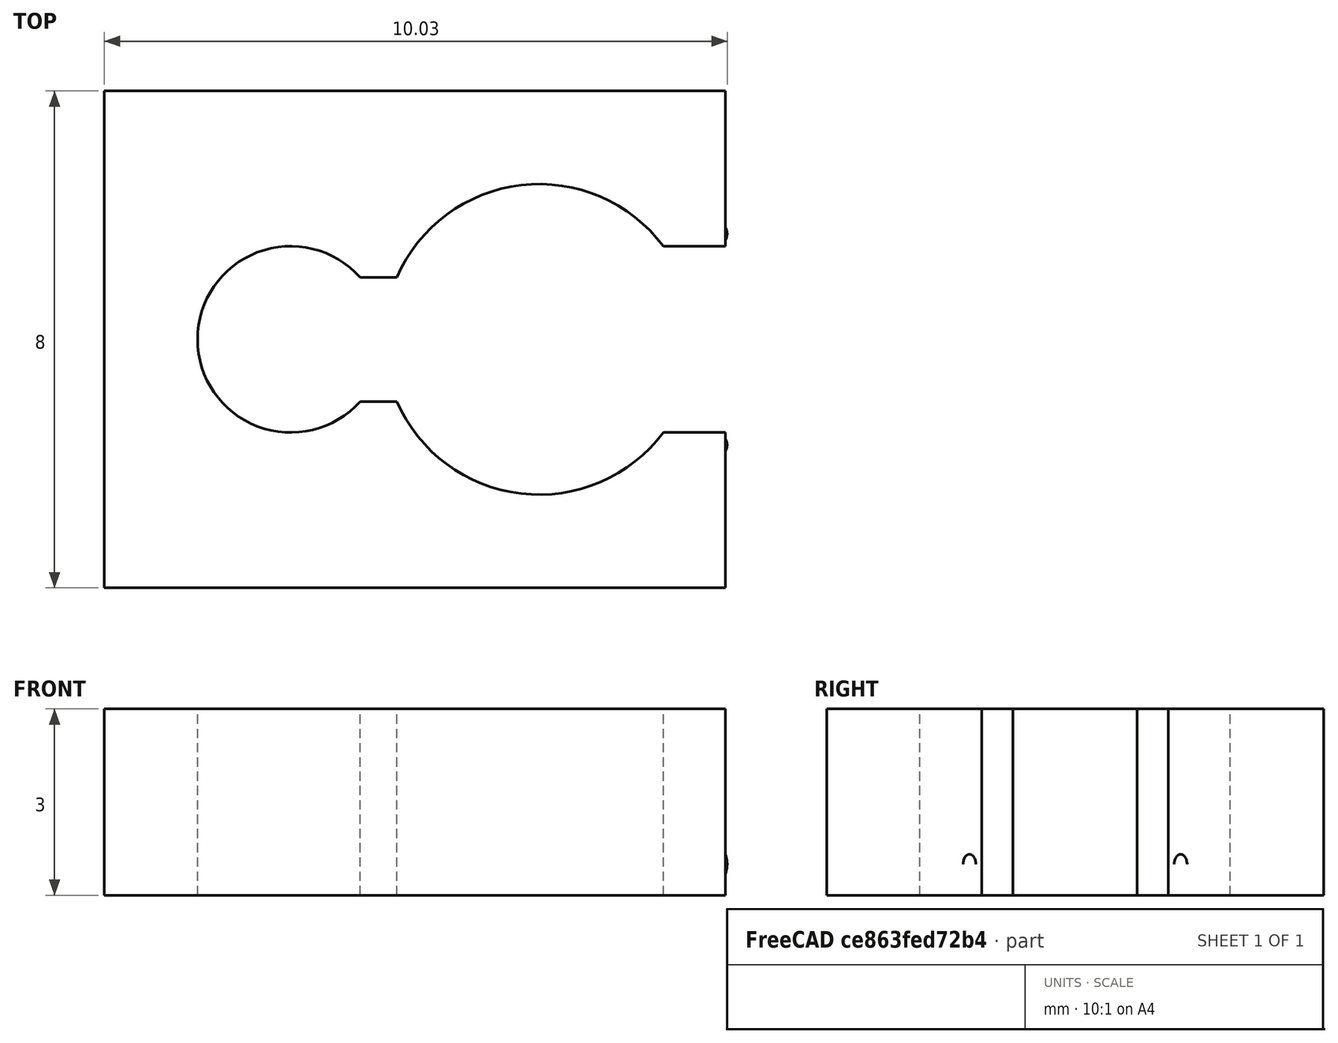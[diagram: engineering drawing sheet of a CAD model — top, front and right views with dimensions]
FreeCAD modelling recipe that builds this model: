
FCSTD DOCUMENT  (FreeCAD 0.16R)
Label: Auriculares Edu V3
License: All rights reserved
LicenseURL: http://en.wikipedia.org/wiki/All_rights_reserved
objects: Part::Cut×8, Part::Box×5, Part::Cylinder×4, Part::Torus×2, Part::MultiFuse×2, PartDesign::Fillet×1
note: 22 computed .brp shape members not serialized (recipe doc carries the construction recipe); baked Part::Feature solids carry a one-line shape summary decoded from their .brp

FEATURE [Part::Torus] Torus  label="Toro"
  Angle1 = -180
  Angle2 = 180
  Angle3 = 360
  Placement = pos=(-1,0,0) rot=(0,0,1;0rad)
  Radius1 = 3
  Radius2 = 0.5
FEATURE [Part::Torus] Torus001  label="Toro001"
  Angle1 = -180
  Angle2 = 180
  Angle3 = 360
  Placement = pos=(-5,0,0) rot=(0,0,1;0rad)
  Radius1 = 2
  Radius2 = 0.5
FEATURE [Part::MultiFuse] Fusion
  Shapes = -> [Torus001,Torus]
FEATURE [Part::Cylinder] Cylinder  label="Cilindro"
  Angle = 360
  Height = 10
  Placement = pos=(-5,0,-4) rot=(0,0,1;0rad)
  Radius = 1.5
FEATURE [Part::Cut] Cut
  Base = -> Fusion
  Tool = -> Cylinder
FEATURE [Part::Cylinder] Cylinder001  label="Cilindro001"
  Angle = 360
  Height = 10
  Placement = pos=(-1,0,-9) rot=(0,0,1;0rad)
  Radius = 2.5
FEATURE [Part::Cut] Cut001
  Base = -> Cut
  Tool = -> Cylinder001
FEATURE [Part::Box] Box  label="Cubo"
  Height = 5
  Length = 3
  Placement = pos=(-4,-0.5,-3) rot=(0,0,1;0rad)
  Width = 1
FEATURE [Part::Cut] Cut002
  Base = -> Cut001
  Tool = -> Box
FEATURE [Part::Box] Box001  label="Cubo001"
  Height = 10
  Length = 4
  Placement = pos=(0,-1.5,-6) rot=(0,0,1;0rad)
  Width = 3
FEATURE [Part::Cut] Cut003
  Base = -> Cut002
  Tool = -> Box001
FEATURE [PartDesign::Fillet] Fillet
  Base = -> Cut003 [Edge34,Edge14,Edge23,Edge25]
  Radius = 0.5
FEATURE [Part::Box] Box002  label="Cubo002"
  Height = 3
  Length = 10
  Placement = pos=(-8,-4,-0.5) rot=(0,0,1;0rad)
  Width = 8
FEATURE [Part::Cylinder] Cylinder002  label="Cilindro002"
  Angle = 360
  Height = 10
  Placement = pos=(-5,0,-1) rot=(0,0,1;0rad)
  Radius = 1.5
FEATURE [Part::MultiFuse] Fusion001
  Shapes = -> [Box002,Fillet]
FEATURE [Part::Cylinder] Cylinder003  label="Cilindro003"
  Angle = 360
  Height = 10
  Placement = pos=(-1,0,-1) rot=(0,0,1;0rad)
  Radius = 2.5
FEATURE [Part::Cut] Cut004
  Base = -> Fusion001
  Tool = -> Cylinder002
FEATURE [Part::Cut] Cut005
  Base = -> Cut004
  Tool = -> Cylinder003
FEATURE [Part::Box] Box003  label="Cubo003"
  Height = 10
  Length = 9
  Placement = pos=(0,-1.5,-3) rot=(0,0,1;0rad)
  Width = 3
FEATURE [Part::Cut] Cut006
  Base = -> Cut005
  Tool = -> Box003
FEATURE [Part::Box] Box004  label="Cubo004"
  Height = 10
  Length = 9
  Placement = pos=(-5,-1,-2) rot=(0,0,1;0rad)
  Width = 2
FEATURE [Part::Cut] Cut007
  Base = -> Cut006
  Tool = -> Box004
